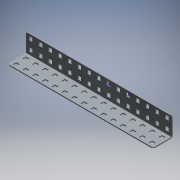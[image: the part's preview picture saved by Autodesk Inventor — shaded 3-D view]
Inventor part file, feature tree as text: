
AUTODESK INVENTOR PART (.ipt)
format: ipt  version: 2018 (Build 220112000, 112)  size: 662,528 bytes
history: native  units: mm (DEFAULTED — no unit token found)
features: other x64, extrude x60, sketch x7, sheet_metal_op x3, pattern_linear x2
ambient origin geometry x8: Origin, YZ Plane, XZ Plane, XY Plane, X Axis, Y Axis, Z Axis, Center Point
bodies: Solid1 (feature_tree)
feature tree (136):
  sheet_metal_op  "Face1"
  sheet_metal_op  "Flange1"
  other  "Corner Chamfer1"
  pattern_linear  "Rectangular Pattern1"  Count1=15 Spacing1=12.7mm
  pattern_linear  "Rectangular Pattern2"  Spacing1=0.8636mm  [1 undecoded]
  sketch  "Sketch6"  dims[d5=24.13mm d6=150.0mm d8=12.7mm d9=10.0mm d11=25.4mm]
  sketch  "Sketch7"  dims[d13=4.064mm d14=0.8636mm d15=1.27mm d16=0.635mm d17=2.54mm d18=0.8636mm d19=24.13mm d20=90.0deg d21=0.8636mm d22=1.905mm d23=6.35mm d24=45.0deg d25=4.572mm d26=4.572mm d27=8.128mm d28=4.064mm d29=2.794mm d30=4.572mm d31=4.064mm d32=150.0mm d34=12.7mm d35=10.0mm d37=25.4mm d39=1.27mm d40=0.0mm d41=25.4mm d42=0.0mm d43=150.0mm d45=12.7mm d46=20.0mm d48=12.7mm d49=0.0mm d50=0.0mm d51=0.0mm d52=0.0mm d53=0.0mm d54=0.0mm d55=0.0mm d56=0.0mm d57=0.0mm d58=0.0mm d59=0.0mm d60=0.0mm d61=0.0mm d62=0.0mm d63=0.0mm d64=0.0mm d65=0.0mm d66=0.0mm d67=0.0mm d68=0.0mm d69=0.0mm d70=0.0mm d71=0.0mm d72=0.0mm d73=0.0mm d74=0.0mm d75=0.0mm d76=0.0mm d77=0.0mm d78=0.0mm d79=0.0mm d80=0.0mm d81=0.0mm d82=0.0mm d83=0.0mm d84=0.0mm d85=0.0mm d86=0.0mm d87=0.0mm d88=0.0mm d89=0.0mm d90=0.0mm d91=0.0mm d92=0.0mm d93=0.0mm d94=0.0mm d95=0.0mm d96=0.0mm d97=0.0mm d98=0.0mm d99=0.0mm d100=0.0mm d101=0.0mm d102=0.0mm d103=0.0mm d104=0.0mm d105=0.0mm d106=0.0mm d107=0.0mm d108=0.0mm d109=25.4mm d110=0.0mm d111=150.0mm d113=12.7mm d114=20.0mm d116=12.7mm d117=0.0mm d118=0.0mm d119=0.0mm d120=0.0mm d121=0.0mm d122=0.0mm d123=0.0mm d124=0.0mm d125=0.0mm d126=0.0mm d127=0.0mm d128=0.0mm d129=0.0mm d130=0.0mm d131=0.0mm d132=0.0mm d133=0.0mm d134=0.0mm d135=0.0mm d136=0.0mm d137=0.0mm d138=0.0mm d139=0.0mm d140=0.0mm d141=0.0mm d142=0.0mm d143=0.0mm d144=0.0mm d145=0.0mm d146=0.0mm d147=0.0mm d148=0.0mm d149=0.0mm d150=0.0mm d151=0.0mm d152=0.0mm d153=0.0mm d154=0.0mm d155=0.0mm d156=0.0mm d157=0.0mm d158=0.0mm d159=0.0mm d160=0.0mm d161=0.0mm d162=0.0mm d163=0.0mm d164=0.0mm d165=0.0mm d166=0.0mm d167=0.0mm d168=0.0mm d169=0.0mm d170=0.0mm d171=0.0mm d172=0.0mm d173=0.0mm d174=0.0mm d175=0.0mm d176=0.0mm d177=1.27mm]
  sketch  "Sketch1"  dims[d0=2.794mm]
  other  "Plate1"
  sketch  "Sketch2"  dims[d1=8.128mm]
  other  "Plate2"
  sheet_metal_op  "Bend1"
  sketch  "Sketch3"  dims[d2=4.572mm]
  sketch  "Sketch4"  dims[d3=4.572mm]
  other  "Srf1"
  other  "Srf2"
  other  "Srf3"
  other  "Srf4"
  other  "Srf5"
  other  "Srf6"
  other  "Srf7"
  other  "Srf8"
  other  "Srf9"
  other  "Srf10"
  other  "Srf11"
  other  "Srf12"
  other  "Srf13"
  other  "Srf14"
  other  "Srf15"
  other  "Srf16"
  other  "Srf17"
  other  "Srf18"
  other  "Srf19"
  other  "Srf20"
  other  "Srf21"
  other  "Srf22"
  other  "Srf23"
  other  "Srf24"
  other  "Srf25"
  other  "Srf26"
  other  "Srf27"
  other  "Srf28"
  other  "Srf29"
  other  "Srf30"
  sketch  "Sketch5"  dims[d4=4.572mm]
  other  "Srf31"
  other  "Srf32"
  other  "Srf33"
  other  "Srf34"
  other  "Srf35"
  other  "Srf36"
  other  "Srf37"
  other  "Srf38"
  other  "Srf39"
  other  "Srf40"
  other  "Srf41"
  other  "Srf42"
  other  "Srf43"
  other  "Srf44"
  other  "Srf45"
  other  "Srf46"
  other  "Srf47"
  other  "Srf48"
  other  "Srf49"
  other  "Srf50"
  other  "Srf51"
  other  "Srf52"
  other  "Srf53"
  other  "Srf54"
  other  "Srf55"
  other  "Srf56"
  other  "Srf57"
  other  "Srf58"
  other  "Srf59"
  other  "Srf60"
  other  "Cut1"
  extrude  "ExtrusionSrf1"  Depth=1.27mm
  extrude  "ExtrusionSrf31"  Depth=1.27mm
  extrude  "ExtrusionSrf2"  Depth=1.27mm
  extrude  "ExtrusionSrf3"  Depth=0.8636mm
  extrude  "ExtrusionSrf4"  Depth=24.13mm TaperAngle=90.0deg
  extrude  "ExtrusionSrf5"  Depth=1.27mm TaperAngle=45.0deg
  extrude  "ExtrusionSrf6"  Depth=4.572mm
  extrude  "ExtrusionSrf7"  Depth=4.572mm
  extrude  "ExtrusionSrf8"  Depth=8.128mm
  extrude  "ExtrusionSrf9"  Depth=4.064mm
  extrude  "ExtrusionSrf10"  Depth=2.794mm
  extrude  "ExtrusionSrf11"  Depth=4.572mm
  extrude  "ExtrusionSrf12"  Depth=4.064mm
  extrude  "ExtrusionSrf13"  Depth=12.7mm
  extrude  "ExtrusionSrf14"  Depth=1.27mm
  extrude  "ExtrusionSrf15"  TaperAngle=0.0deg  [1 undecoded]
  extrude  "ExtrusionSrf16"  Depth=25.4mm TaperAngle=0.0deg
  extrude  "ExtrusionSrf17"  Depth=12.7mm
  extrude  "ExtrusionSrf18"  Depth=12.7mm
  extrude  "ExtrusionSrf19"  TaperAngle=0.0deg  [1 undecoded]
  extrude  "ExtrusionSrf20"  TaperAngle=0.0deg  [1 undecoded]
  extrude  "ExtrusionSrf21"  TaperAngle=0.0deg  [1 undecoded]
  extrude  "ExtrusionSrf22"  TaperAngle=0.0deg  [1 undecoded]
  extrude  "ExtrusionSrf23"  TaperAngle=0.0deg  [1 undecoded]
  extrude  "ExtrusionSrf24"  TaperAngle=0.0deg  [1 undecoded]
  extrude  "ExtrusionSrf25"  TaperAngle=0.0deg  [1 undecoded]
  extrude  "ExtrusionSrf26"  TaperAngle=0.0deg  [1 undecoded]
  extrude  "ExtrusionSrf27"  TaperAngle=0.0deg  [1 undecoded]
  extrude  "ExtrusionSrf28"  TaperAngle=0.0deg  [1 undecoded]
  extrude  "ExtrusionSrf29"  TaperAngle=0.0deg  [1 undecoded]
  extrude  "ExtrusionSrf30"  TaperAngle=0.0deg  [1 undecoded]
  extrude  "ExtrusionSrf32"  TaperAngle=0.0deg  [1 undecoded]
  extrude  "ExtrusionSrf33"  TaperAngle=0.0deg  [1 undecoded]
  extrude  "ExtrusionSrf34"  TaperAngle=0.0deg  [1 undecoded]
  extrude  "ExtrusionSrf35"  TaperAngle=0.0deg  [1 undecoded]
  extrude  "ExtrusionSrf36"  TaperAngle=0.0deg  [1 undecoded]
  extrude  "ExtrusionSrf37"  TaperAngle=0.0deg  [1 undecoded]
  extrude  "ExtrusionSrf38"  TaperAngle=0.0deg  [1 undecoded]
  extrude  "ExtrusionSrf39"  TaperAngle=0.0deg  [1 undecoded]
  extrude  "ExtrusionSrf40"  TaperAngle=0.0deg  [1 undecoded]
  extrude  "ExtrusionSrf41"  TaperAngle=0.0deg  [1 undecoded]
  extrude  "ExtrusionSrf42"  TaperAngle=0.0deg  [1 undecoded]
  extrude  "ExtrusionSrf43"  TaperAngle=0.0deg  [1 undecoded]
  extrude  "ExtrusionSrf44"  TaperAngle=0.0deg  [1 undecoded]
  extrude  "ExtrusionSrf45"  TaperAngle=0.0deg  [1 undecoded]
  extrude  "ExtrusionSrf46"  TaperAngle=0.0deg  [1 undecoded]
  extrude  "ExtrusionSrf47"  TaperAngle=0.0deg  [1 undecoded]
  extrude  "ExtrusionSrf48"  TaperAngle=0.0deg  [1 undecoded]
  extrude  "ExtrusionSrf49"  TaperAngle=0.0deg  [1 undecoded]
  extrude  "ExtrusionSrf50"  TaperAngle=0.0deg  [1 undecoded]
  extrude  "ExtrusionSrf51"  TaperAngle=0.0deg  [1 undecoded]
  extrude  "ExtrusionSrf52"  TaperAngle=0.0deg  [1 undecoded]
  extrude  "ExtrusionSrf53"  TaperAngle=0.0deg  [1 undecoded]
  extrude  "ExtrusionSrf54"  TaperAngle=0.0deg  [1 undecoded]
  extrude  "ExtrusionSrf55"  TaperAngle=0.0deg  [1 undecoded]
  extrude  "ExtrusionSrf56"  TaperAngle=0.0deg  [1 undecoded]
  extrude  "ExtrusionSrf57"  TaperAngle=0.0deg  [1 undecoded]
  extrude  "ExtrusionSrf58"  TaperAngle=0.0deg  [1 undecoded]
  extrude  "ExtrusionSrf59"  TaperAngle=0.0deg  [1 undecoded]
  extrude  "ExtrusionSrf60"  TaperAngle=0.0deg  [1 undecoded]
note: 43 required parameter values undecoded (feature->parameter linkage not recoverable at this tier; creation-order binding heuristic only, values carry confidence <= 0.55)
